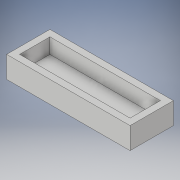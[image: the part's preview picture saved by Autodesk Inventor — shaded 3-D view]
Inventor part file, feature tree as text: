
AUTODESK INVENTOR PART (.ipt)
format: ipt  version: 2018.1 (Build 221171000, 171)  size: 98,304 bytes
history: native  units: mm
features: other x1, extrude x1, shell x1, sketch x1
ambient origin geometry x8: Origin, YZ Plane, XZ Plane, XY Plane, X Axis, Y Axis, Z Axis, Center Point
bodies: Body1 (feature_tree)
feature tree (4):
  other  "ソリッド1"
  extrude  "押し出し1"  Depth=20.0mm
  shell  "シェル2"  Thickness=57.0mm
  sketch  "スケッチ1"
